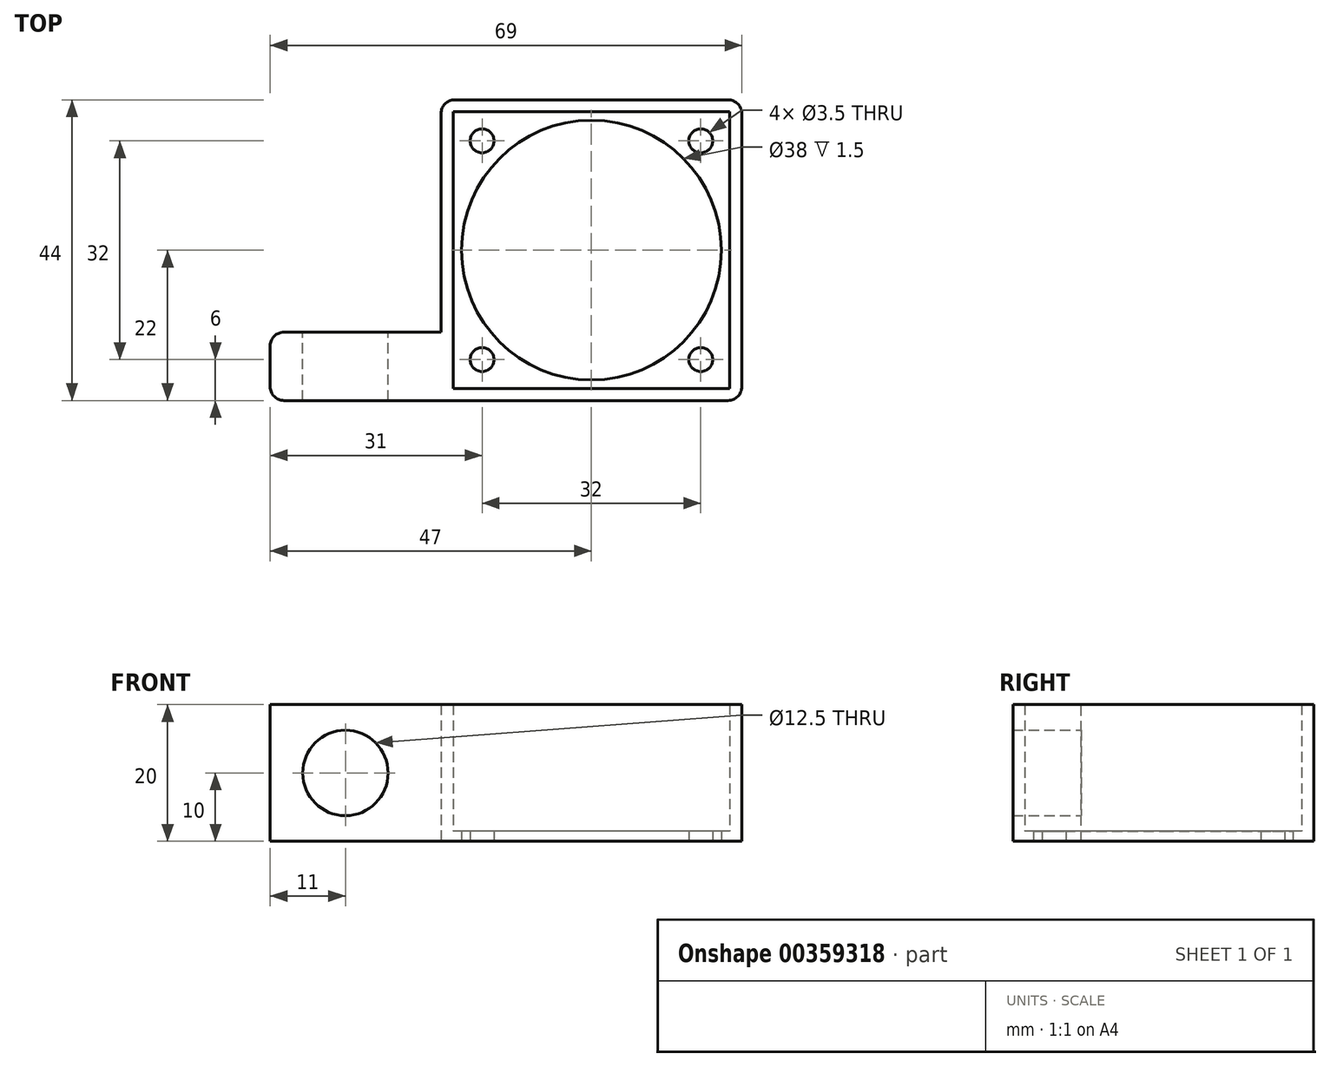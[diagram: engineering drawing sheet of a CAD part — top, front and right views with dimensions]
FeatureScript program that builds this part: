
annotation { "Feature Type Name" : "Feature", "Feature Type Description" : "" }
export const myFeature = defineFeature(function(context is Context, id is Id, definition is map)
    precondition{}
    {
        {
            var Q0;
            Q0=qCreatedBy(makeId("Top.planeOp"),FACE);
            var sketch = newSketch(context, id + "F0", { "sketchPlane" : qUnion([Q0])});
            skLineSegment(sketch, "E0.bottom", {"start": v(22, 22) * mm, "end": v(-22, 22) * mm});
            skLineSegment(sketch, "E0.top", {"start": v(22, -22) * mm, "end": v(-22, -22) * mm});
            skLineSegment(sketch, "E0.left", {"start": v(22, 22) * mm, "end": v(22, -22) * mm});
            skLineSegment(sketch, "E0.right", {"start": v(-22, 22) * mm, "end": v(-22, -22) * mm});
            skPoint(sketch, "E0.middle", {"position": v(0, 0) * mm});
            skLineSegment(sketch, "E1.bottom", {"start": v(20.25, 20.25) * mm, "end": v(-20.25, 20.25) * mm});
            skLineSegment(sketch, "E1.top", {"start": v(20.25, -20.25) * mm, "end": v(-20.25, -20.25) * mm});
            skLineSegment(sketch, "E1.left", {"start": v(20.25, 20.25) * mm, "end": v(20.25, -20.25) * mm});
            skLineSegment(sketch, "E1.right", {"start": v(-20.25, 20.25) * mm, "end": v(-20.25, -20.25) * mm});
            skCircle(sketch, "E2", {"center": v(-16, 16) * mm, "radius": 1.75 * mm});
            skCircle(sketch, "E3", {"center": v(16, 16) * mm, "radius": 1.75 * mm});
            skCircle(sketch, "E4", {"center": v(-16, -16) * mm, "radius": 1.75 * mm});
            skCircle(sketch, "E5", {"center": v(16, -16) * mm, "radius": 1.75 * mm});
            skCircle(sketch, "E6", {"center": v(0, 0) * mm, "radius": 19 * mm});
            skSolve(sketch);
        }
        {
            var Q0;
            Q0=makeQuery(id+"F0.imprint","IMPRINT",FACE,{"disambiguationData":[TD([[makeQuery(id+"F0.imprint","IMPRINT",EDGE,{"derivedFrom":sQuery(id+"F0.wireOp",EDGE,"E0.bottom")}),1.0]])]});
            extrude(context, id + "F1", {"entities" : qUnion([Q0]), "depth" : 20 * mm});
        }
        {
            var Q0;
            Q0=makeQuery(id+"F0.imprint","IMPRINT",FACE,{"disambiguationData":[TD([[makeQuery(id+"F0.imprint","IMPRINT",EDGE,{"derivedFrom":sQuery(id+"F0.wireOp",EDGE,"E1.bottom")}),1.0]])]});
            extrude(context, id + "F2", {"entities" : qUnion([Q0]), "operationType" : NewBodyOperationType.ADD, "depth" : 1.5 * mm});
        }
        {
            var Q0;
            Q0=makeQuery(id+"F1.opExtrude","SWEPT_FACE",FACE,{"disambiguationData":[OSD([sQuery(id+"F0.wireOp",EDGE,"E0.right")])]});
            var sketch = newSketch(context, id + "F3", { "sketchPlane" : qUnion([Q0])});
            skLineSegment(sketch, "E7.bottom", {"start": v(22, 0) * mm, "end": v(12, 0) * mm});
            skLineSegment(sketch, "E7.top", {"start": v(22, 20) * mm, "end": v(12, 20) * mm});
            skLineSegment(sketch, "E7.left", {"start": v(22, 0) * mm, "end": v(22, 20) * mm});
            skLineSegment(sketch, "E7.right", {"start": v(12, 0) * mm, "end": v(12, 20) * mm});
            skSolve(sketch);
        }
        {
            var Q0;
            Q0=makeQuery(id+"F3.imprint","IMPRINT",FACE,{"disambiguationData":[TD([[makeQuery(id+"F3.imprint","IMPRINT",EDGE,{"derivedFrom":sQuery(id+"F3.wireOp",EDGE,"E7.bottom")}),1.0]])]});
            extrude(context, id + "F4", {"entities" : qUnion([Q0]), "operationType" : NewBodyOperationType.ADD, "depth" : 25 * mm});
        }
        {
            var Q0;
            Q0=makeQuery(id+"F4.opExtrude","SWEPT_FACE",FACE,{"disambiguationData":[OSD([sQuery(id+"F3.wireOp",EDGE,"E7.right")])]});
            var sketch = newSketch(context, id + "F5", { "sketchPlane" : qUnion([Q0])});
            skCircle(sketch, "E8", {"center": v(36, 10) * mm, "radius": 6.25 * mm});
            skSolve(sketch);
        }
        {
            var Q0;
            Q0=makeQuery(id+"F5.imprint","IMPRINT",FACE,{"disambiguationData":[TD([[makeQuery(id+"F5.imprint","IMPRINT",EDGE,{"derivedFrom":sQuery(id+"F5.wireOp",EDGE,"E8")}),1.0]])]});
            extrude(context, id + "F6", {"entities" : qUnion([Q0]), "operationType" : NewBodyOperationType.REMOVE, "oppositeDirection" : true, "depth" : 10 * mm});
        }
        {
            var Q0;
            Q0=makeQuery(id+"F4.opExtrude","CAP_EDGE",EDGE,{"disambiguationData":[OSD([sQuery(id+"F3.wireOp",EDGE,"E7.right")])],"isStart":true});
            var Q1;
            Q1=makeQuery(id+"F1.opExtrude","SWEPT_EDGE",EDGE,{"disambiguationData":[OSD([sQuery(id+"F0.wireOp",EDGE,"E0.bottom"),sQuery(id+"F0.wireOp",EDGE,"E0.right")])]});
            var Q2;
            Q2=makeQuery(id+"F1.opExtrude","SWEPT_EDGE",EDGE,{"disambiguationData":[OSD([sQuery(id+"F0.wireOp",EDGE,"E0.bottom"),sQuery(id+"F0.wireOp",EDGE,"E0.left")])]});
            var Q3;
            Q3=makeQuery(id+"F1.opExtrude","SWEPT_EDGE",EDGE,{"disambiguationData":[OSD([sQuery(id+"F0.wireOp",EDGE,"E0.top"),sQuery(id+"F0.wireOp",EDGE,"E0.left")])]});
            var Q4;
            Q4=makeQuery(id+"F4.opExtrude","CAP_EDGE",EDGE,{"disambiguationData":[OSD([sQuery(id+"F3.wireOp",EDGE,"E7.right")])],"isStart":false});
            var Q5;
            Q5=makeQuery(id+"F4.opExtrude","CAP_EDGE",EDGE,{"disambiguationData":[OSD([sQuery(id+"F3.wireOp",EDGE,"E7.left")])],"isStart":false});
            fillet(context, id + "F7", {"entities" : qUnion([Q0, Q1, Q2, Q3, Q4, Q5]), "radius" : 2 * mm, "tangentPropagation" : true, "allowEdgeOverflow" : false});
        }
    });
